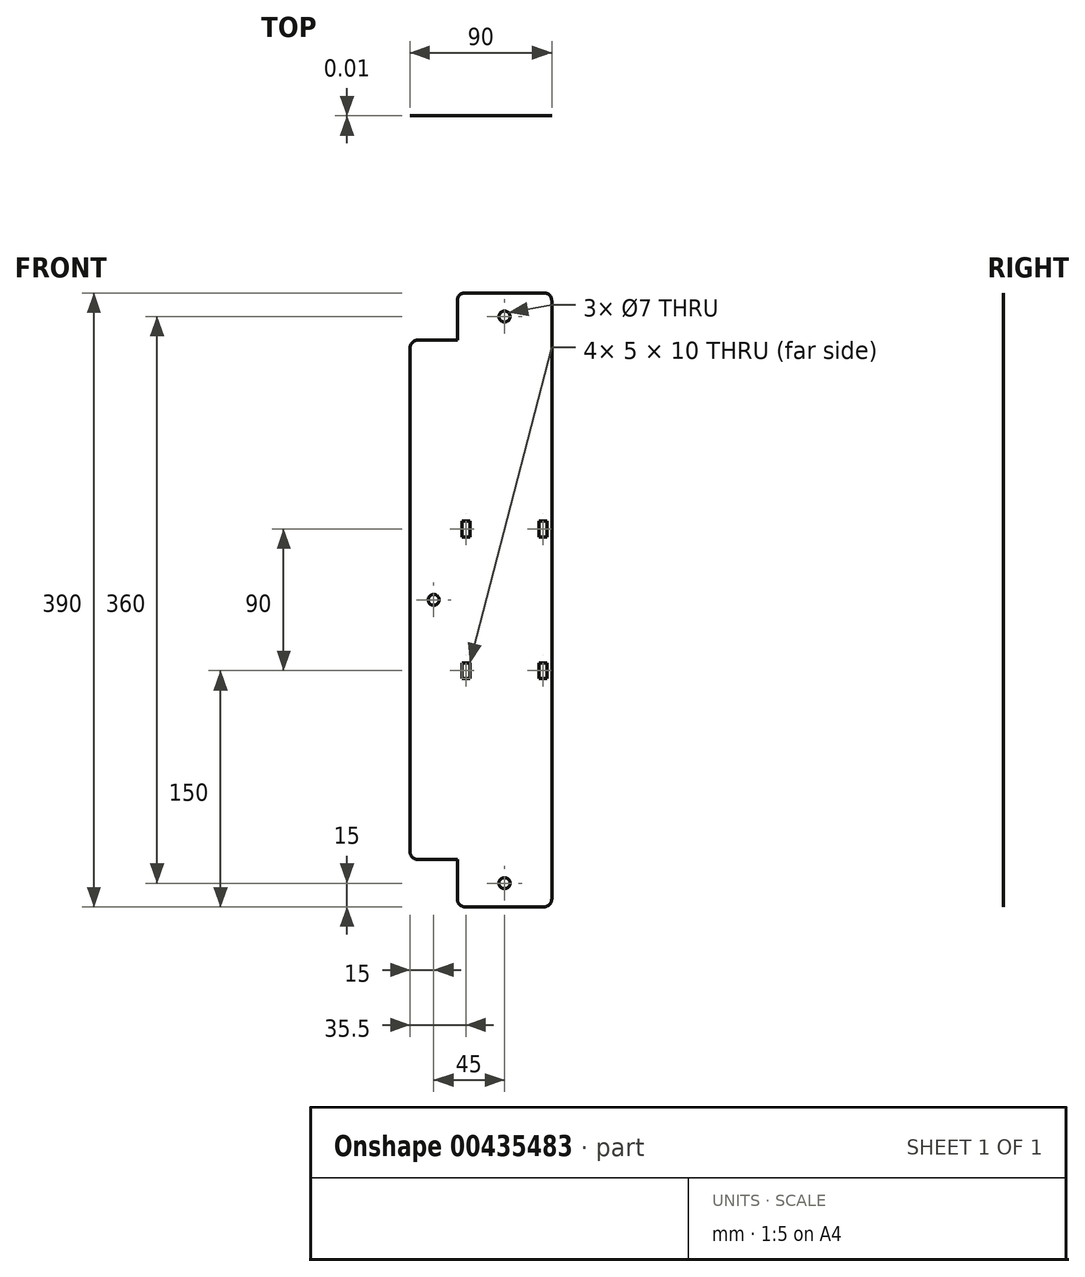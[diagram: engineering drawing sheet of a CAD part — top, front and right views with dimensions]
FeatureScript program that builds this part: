
annotation { "Feature Type Name" : "Feature", "Feature Type Description" : "" }
export const myFeature = defineFeature(function(context is Context, id is Id, definition is map)
    precondition{}
    {
        {
            var Q0;
            Q0=qCreatedBy(makeId("Front.planeOp"),FACE);
            var sketch = newSketch(context, id + "F0", { "sketchPlane" : qUnion([Q0])});
            skLineSegment(sketch, "E0", {"start": v(0, 5) * mm, "end": v(0, 385) * mm});
            skLineSegment(sketch, "E1", {"start": v(5, 390) * mm, "end": v(75, 390) * mm});
            skLineSegment(sketch, "E2", {"start": v(80, 360) * mm, "end": v(85.5, 360) * mm});
            skLineSegment(sketch, "E3", {"start": v(5, 0) * mm, "end": v(75, 0) * mm});
            skLineSegment(sketch, "E4", {"start": v(80, 5) * mm, "end": v(80, 30) * mm});
            skLineSegment(sketch, "E5", {"start": v(80, 30) * mm, "end": v(105, 30) * mm});
            skLineSegment(sketch, "E6", {"start": v(110, 35) * mm, "end": v(110, 355) * mm});
            skLineSegment(sketch, "E7", {"start": v(80, 375) * mm, "end": v(0, 375) * mm, "construction": true});
            skLineSegment(sketch, "E8", {"start": v(80, 15) * mm, "end": v(0, 15) * mm, "construction": true});
            skCircle(sketch, "E9", {"center": v(40, 375) * mm, "radius": 3.5 * mm});
            skCircle(sketch, "E10", {"center": v(40, 15) * mm, "radius": 3.5 * mm});
            skLineSegment(sketch, "E11", {"start": v(40, 195) * mm, "end": v(40, 245) * mm, "construction": true});
            skLineSegment(sketch, "E12", {"start": v(40, 245) * mm, "end": v(8.5, 245) * mm, "construction": true});
            skLineSegment(sketch, "E13.bottom", {"start": v(8.5, 245) * mm, "end": v(3.5, 245) * mm});
            skLineSegment(sketch, "E13.top", {"start": v(8.5, 235) * mm, "end": v(3.5, 235) * mm});
            skLineSegment(sketch, "E13.left", {"start": v(8.5, 245) * mm, "end": v(8.5, 235) * mm});
            skLineSegment(sketch, "E13.right", {"start": v(3.5, 245) * mm, "end": v(3.5, 235) * mm});
            skLineSegment(sketch, "E14", {"start": v(40, 245) * mm, "end": v(71.5, 245) * mm, "construction": true});
            skLineSegment(sketch, "E15.bottom", {"start": v(71.5, 245) * mm, "end": v(76.5, 245) * mm});
            skLineSegment(sketch, "E15.top", {"start": v(71.5, 235) * mm, "end": v(76.5, 235) * mm});
            skLineSegment(sketch, "E15.left", {"start": v(71.5, 245) * mm, "end": v(71.5, 235) * mm});
            skLineSegment(sketch, "E15.right", {"start": v(76.5, 245) * mm, "end": v(76.5, 235) * mm});
            skLineSegment(sketch, "E16", {"start": v(40, 195) * mm, "end": v(40, 145) * mm, "construction": true});
            skLineSegment(sketch, "E17", {"start": v(40, 145) * mm, "end": v(71.5, 145) * mm, "construction": true});
            skLineSegment(sketch, "E18", {"start": v(40, 145) * mm, "end": v(8.5, 145) * mm, "construction": true});
            skLineSegment(sketch, "E19.bottom", {"start": v(8.5, 145) * mm, "end": v(3.5, 145) * mm});
            skLineSegment(sketch, "E19.top", {"start": v(8.5, 155) * mm, "end": v(3.5, 155) * mm});
            skLineSegment(sketch, "E19.left", {"start": v(8.5, 145) * mm, "end": v(8.5, 155) * mm});
            skLineSegment(sketch, "E19.right", {"start": v(3.5, 145) * mm, "end": v(3.5, 155) * mm});
            skLineSegment(sketch, "E20.bottom", {"start": v(71.5, 145) * mm, "end": v(76.5, 145) * mm});
            skLineSegment(sketch, "E20.top", {"start": v(71.5, 155) * mm, "end": v(76.5, 155) * mm});
            skLineSegment(sketch, "E20.left", {"start": v(71.5, 145) * mm, "end": v(71.5, 155) * mm});
            skLineSegment(sketch, "E20.right", {"start": v(76.5, 145) * mm, "end": v(76.5, 155) * mm});
            skLineSegment(sketch, "E21", {"start": v(0, 195) * mm, "end": v(40, 195) * mm, "construction": true});
            skLineSegment(sketch, "E22", {"start": v(80, 360) * mm, "end": v(80, 30) * mm, "construction": true});
            skLineSegment(sketch, "E23", {"start": v(110, 195) * mm, "end": v(95, 195) * mm, "construction": true});
            skPoint(sketch, "E23.endSnap0", {"position": v(110, 195) * mm});
            skCircle(sketch, "E24", {"center": v(95, 195) * mm, "radius": 3.5 * mm});
            skPoint(sketch, "E25.visualSharp", {"position": v(0, 390) * mm});
            skArc(sketch, "E25.filletArc", {"start": v(5, 390) * mm, "mid": v(1.46, 388.54) * mm, "end": v(0, 385) * mm});
            skPoint(sketch, "E26.visualSharp", {"position": v(80, 390) * mm});
            skArc(sketch, "E26.filletArc", {"start": v(80, 385) * mm, "mid": v(78.54, 388.54) * mm, "end": v(75, 390) * mm});
            skPoint(sketch, "E27.visualSharp", {"position": v(110, 360) * mm});
            skArc(sketch, "E27.filletArc", {"start": v(110, 355) * mm, "mid": v(108.54, 358.54) * mm, "end": v(105, 360) * mm});
            skPoint(sketch, "E28.visualSharp", {"position": v(80, 360) * mm});
            skPoint(sketch, "E29.visualSharp", {"position": v(110, 30) * mm});
            skArc(sketch, "E29.filletArc", {"start": v(105, 30) * mm, "mid": v(108.54, 31.46) * mm, "end": v(110, 35) * mm});
            skPoint(sketch, "E30.visualSharp", {"position": v(80, 0) * mm});
            skArc(sketch, "E30.filletArc", {"start": v(75, 0) * mm, "mid": v(78.54, 1.46) * mm, "end": v(80, 5) * mm});
            skPoint(sketch, "E31.visualSharp", {"position": v(0, 0) * mm});
            skArc(sketch, "E31.filletArc", {"start": v(0, 5) * mm, "mid": v(1.46, 1.46) * mm, "end": v(5, 0) * mm});
            skLineSegment(sketch, "E32", {"start": v(80, 360) * mm, "end": v(80, 365.5) * mm});
            skLineSegment(sketch, "E33", {"start": v(80, 365.5) * mm, "end": v(80, 385) * mm});
            skLineSegment(sketch, "E34", {"start": v(85.5, 360) * mm, "end": v(105, 360) * mm});
            skLineSegment(sketch, "E35", {"start": v(80, 390) * mm, "end": v(80, 360) * mm});
            skLineSegment(sketch, "E36", {"start": v(80, 360) * mm, "end": v(110, 360) * mm});
            skSolve(sketch);
        }
        {
            var Q0;
            Q0=qCreatedBy(makeId("Front.planeOp"),FACE);
            var sketch = newSketch(context, id + "F1", { "sketchPlane" : qUnion([Q0])});
            skLineSegment(sketch, "E37", {"start": v(0, 5) * mm, "end": v(0, 385) * mm});
            skLineSegment(sketch, "E38", {"start": v(-5, 0) * mm, "end": v(-55, 0) * mm});
            skLineSegment(sketch, "E39", {"start": v(-60, 5) * mm, "end": v(-60, 30) * mm});
            skLineSegment(sketch, "E40", {"start": v(-60, 30) * mm, "end": v(-85, 30) * mm});
            skLineSegment(sketch, "E41", {"start": v(-90, 35) * mm, "end": v(-90, 355) * mm});
            skLineSegment(sketch, "E42", {"start": v(-85, 360) * mm, "end": v(-60, 360) * mm});
            skLineSegment(sketch, "E43", {"start": v(-60, 360) * mm, "end": v(-60, 385) * mm});
            skLineSegment(sketch, "E44", {"start": v(-55, 390) * mm, "end": v(-5, 390) * mm});
            skLineSegment(sketch, "E45", {"start": v(-90, 195) * mm, "end": v(-75, 195) * mm, "construction": true});
            skCircle(sketch, "E46", {"center": v(-75, 195) * mm, "radius": 3.5 * mm});
            skLineSegment(sketch, "E47", {"start": v(-60, 375) * mm, "end": v(0, 375) * mm, "construction": true});
            skCircle(sketch, "E48", {"center": v(-30, 375) * mm, "radius": 3.5 * mm});
            skLineSegment(sketch, "E49", {"start": v(-60, 15) * mm, "end": v(0, 15) * mm, "construction": true});
            skCircle(sketch, "E50", {"center": v(-30, 15) * mm, "radius": 3.5 * mm});
            skLineSegment(sketch, "E51", {"start": v(0, 195) * mm, "end": v(-30, 195) * mm, "construction": true});
            skLineSegment(sketch, "E52", {"start": v(-30, 195) * mm, "end": v(-30, 245) * mm, "construction": true});
            skLineSegment(sketch, "E53", {"start": v(-30, 245) * mm, "end": v(-8, 245) * mm, "construction": true});
            skLineSegment(sketch, "E54", {"start": v(-30, 195) * mm, "end": v(-30, 145) * mm, "construction": true});
            skLineSegment(sketch, "E55", {"start": v(-30, 145) * mm, "end": v(-8, 145) * mm, "construction": true});
            skLineSegment(sketch, "E56", {"start": v(-30, 145) * mm, "end": v(-52, 145) * mm, "construction": true});
            skLineSegment(sketch, "E57", {"start": v(-30, 245) * mm, "end": v(-52, 245) * mm, "construction": true});
            skLineSegment(sketch, "E58.bottom", {"start": v(-52, 245) * mm, "end": v(-57, 245) * mm});
            skLineSegment(sketch, "E58.top", {"start": v(-52, 235) * mm, "end": v(-57, 235) * mm});
            skLineSegment(sketch, "E58.left", {"start": v(-52, 245) * mm, "end": v(-52, 235) * mm});
            skLineSegment(sketch, "E58.right", {"start": v(-57, 245) * mm, "end": v(-57, 235) * mm});
            skLineSegment(sketch, "E59.bottom", {"start": v(-8, 245) * mm, "end": v(-3, 245) * mm});
            skLineSegment(sketch, "E59.top", {"start": v(-8, 235) * mm, "end": v(-3, 235) * mm});
            skLineSegment(sketch, "E59.left", {"start": v(-8, 245) * mm, "end": v(-8, 235) * mm});
            skLineSegment(sketch, "E59.right", {"start": v(-3, 245) * mm, "end": v(-3, 235) * mm});
            skLineSegment(sketch, "E60.bottom", {"start": v(-52, 145) * mm, "end": v(-57, 145) * mm});
            skLineSegment(sketch, "E60.top", {"start": v(-52, 155) * mm, "end": v(-57, 155) * mm});
            skLineSegment(sketch, "E60.left", {"start": v(-52, 145) * mm, "end": v(-52, 155) * mm});
            skLineSegment(sketch, "E60.right", {"start": v(-57, 145) * mm, "end": v(-57, 155) * mm});
            skLineSegment(sketch, "E61.bottom", {"start": v(-8, 145) * mm, "end": v(-3, 145) * mm});
            skLineSegment(sketch, "E61.top", {"start": v(-8, 155) * mm, "end": v(-3, 155) * mm});
            skLineSegment(sketch, "E61.left", {"start": v(-8, 145) * mm, "end": v(-8, 155) * mm});
            skLineSegment(sketch, "E61.right", {"start": v(-3, 145) * mm, "end": v(-3, 155) * mm});
            skPoint(sketch, "E62.visualSharp", {"position": v(0, 390) * mm});
            skArc(sketch, "E62.filletArc", {"start": v(0, 385) * mm, "mid": v(-1.46, 388.54) * mm, "end": v(-5, 390) * mm});
            skPoint(sketch, "E63.visualSharp", {"position": v(-60, 390) * mm});
            skArc(sketch, "E63.filletArc", {"start": v(-55, 390) * mm, "mid": v(-58.54, 388.54) * mm, "end": v(-60, 385) * mm});
            skPoint(sketch, "E64.visualSharp", {"position": v(-90, 360) * mm});
            skArc(sketch, "E64.filletArc", {"start": v(-85, 360) * mm, "mid": v(-88.54, 358.54) * mm, "end": v(-90, 355) * mm});
            skPoint(sketch, "E65.visualSharp", {"position": v(0, 0) * mm});
            skArc(sketch, "E65.filletArc", {"start": v(-5, 0) * mm, "mid": v(-1.46, 1.46) * mm, "end": v(0, 5) * mm});
            skPoint(sketch, "E66.visualSharp", {"position": v(-60, 0) * mm});
            skArc(sketch, "E66.filletArc", {"start": v(-60, 5) * mm, "mid": v(-58.54, 1.46) * mm, "end": v(-55, 0) * mm});
            skPoint(sketch, "E67.visualSharp", {"position": v(-90, 30) * mm});
            skArc(sketch, "E67.filletArc", {"start": v(-90, 35) * mm, "mid": v(-88.54, 31.46) * mm, "end": v(-85, 30) * mm});
            skSolve(sketch);
        }
        {
            var Q0;
            Q0=makeQuery(id+"F1.imprint","IMPRINT",FACE,{"disambiguationData":[TD([[makeQuery(id+"F1.imprint","IMPRINT",EDGE,{"derivedFrom":sQuery(id+"F1.wireOp",EDGE,"E37")}),1.0]])]});
            extrude(context, id + "F2", {"entities" : qUnion([Q0]), "depth" : 3 / 406.4 * mm, "offsetDistance" : 25 * mm});
        }
    });
